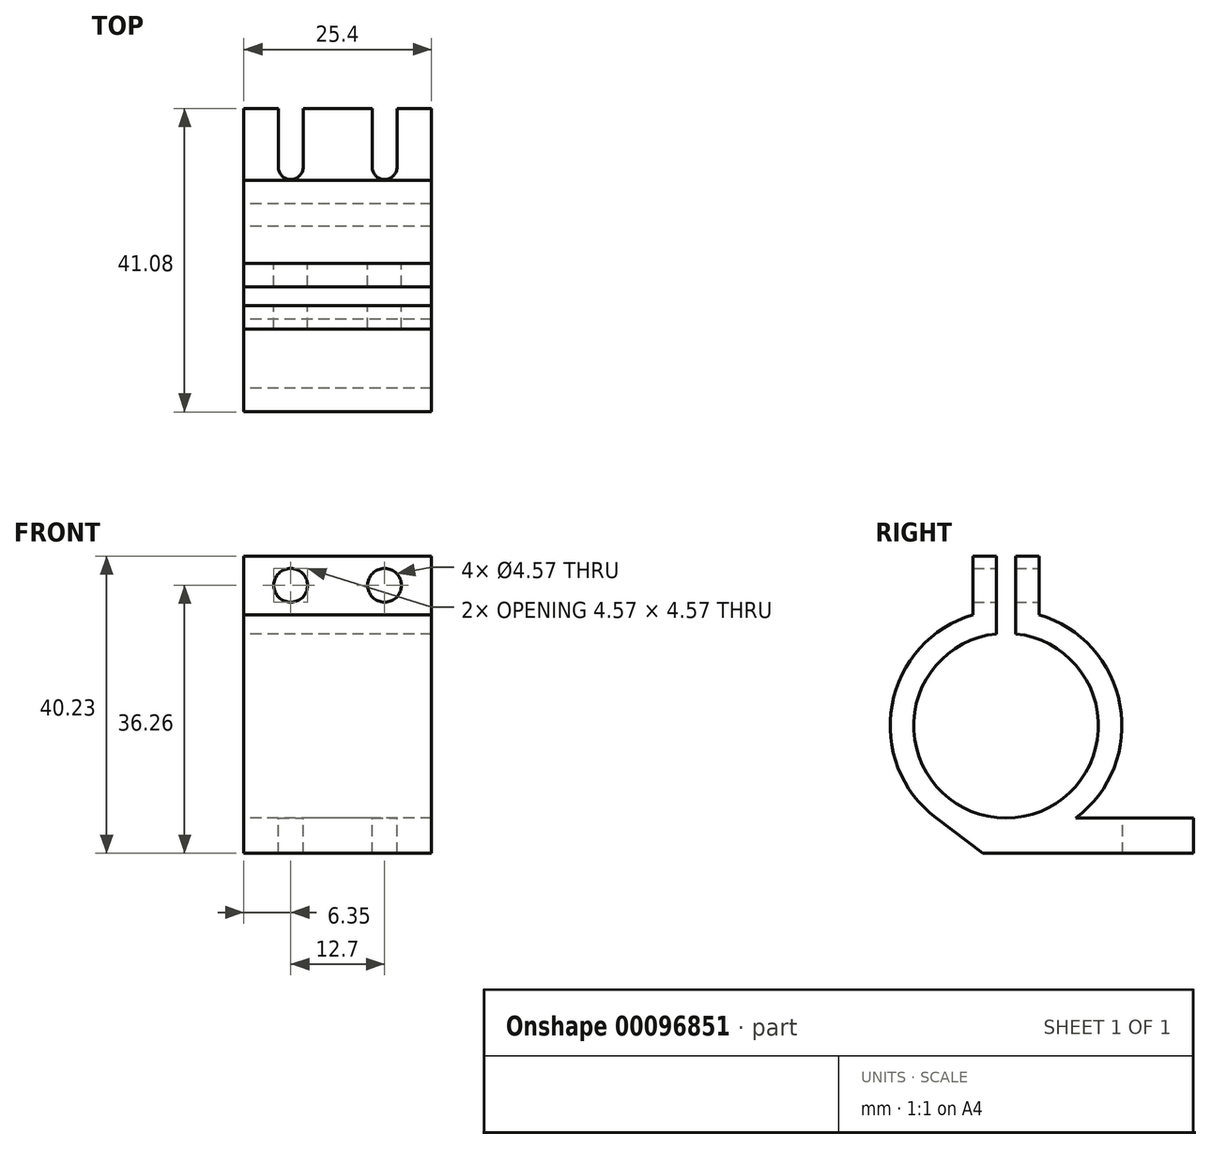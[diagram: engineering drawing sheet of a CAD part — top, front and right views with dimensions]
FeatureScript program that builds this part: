
annotation { "Feature Type Name" : "Feature", "Feature Type Description" : "" }
export const myFeature = defineFeature(function(context is Context, id is Id, definition is map)
    precondition{}
    {
        {
            var Q0;
            Q0=qCreatedBy(makeId("Right.planeOp"),FACE);
            var sketch = newSketch(context, id + "F0", { "sketchPlane" : qUnion([Q0])});
            skArc(sketch, "E0", {"start": v(-1.27, 12.44) * mm, "mid": v(0, -12.5) * mm, "end": v(1.27, 12.44) * mm});
            skLineSegment(sketch, "E1", {"start": v(-1.27, 12.44) * mm, "end": v(-1.27, 22.97) * mm});
            skLineSegment(sketch, "E2", {"start": v(-1.27, 22.97) * mm, "end": v(-4.45, 22.97) * mm});
            skLineSegment(sketch, "E3", {"start": v(-4.45, 22.97) * mm, "end": v(-4.45, 15.03) * mm});
            skLineSegment(sketch, "E4", {"start": v(1.27, 12.44) * mm, "end": v(1.27, 22.97) * mm});
            skLineSegment(sketch, "E5", {"start": v(1.27, 22.97) * mm, "end": v(4.45, 22.97) * mm});
            skLineSegment(sketch, "E6", {"start": v(4.45, 22.97) * mm, "end": v(4.45, 15.03) * mm});
            skArc(sketch, "E7", {"start": v(-4.45, 15.03) * mm, "mid": v(-15.42, 2.8) * mm, "end": v(-9.46, -12.5) * mm});
            skLineSegment(sketch, "E8", {"start": v(-9.46, -12.5) * mm, "end": v(-25.4, -12.5) * mm});
            skLineSegment(sketch, "E9", {"start": v(-25.4, -12.5) * mm, "end": v(-25.4, -17.26) * mm});
            skLineSegment(sketch, "E10", {"start": v(-25.4, -17.26) * mm, "end": v(25.4, -17.26) * mm});
            skLineSegment(sketch, "E11", {"start": v(25.4, -17.26) * mm, "end": v(25.4, -12.5) * mm});
            skLineSegment(sketch, "E12", {"start": v(25.4, -12.5) * mm, "end": v(9.46, -12.5) * mm});
            skArc(sketch, "E13", {"start": v(4.45, 15.03) * mm, "mid": v(15.42, 2.8) * mm, "end": v(9.46, -12.5) * mm});
            skSolve(sketch);
        }
        {
            var Q0;
            Q0 = qSketchRegion(id + "F0", true);
            extrude(context, id + "F1", {"entities" : qUnion([Q0]), "depth" : 25.4 * mm});
        }
        {
            var Q0;
            Q0=makeQuery(id+"F1.opExtrude","CAP_FACE",FACE,{"disambiguationData":[OSD([sQuery(id+"F0.wireOp",EDGE,"E0"),sQuery(id+"F0.wireOp",EDGE,"E1"),sQuery(id+"F0.wireOp",EDGE,"E2"),sQuery(id+"F0.wireOp",EDGE,"E3"),sQuery(id+"F0.wireOp",EDGE,"E4"),sQuery(id+"F0.wireOp",EDGE,"E5"),sQuery(id+"F0.wireOp",EDGE,"E6"),sQuery(id+"F0.wireOp",EDGE,"E7"),sQuery(id+"F0.wireOp",EDGE,"E8"),sQuery(id+"F0.wireOp",EDGE,"E9"),sQuery(id+"F0.wireOp",EDGE,"E10"),sQuery(id+"F0.wireOp",EDGE,"E11"),sQuery(id+"F0.wireOp",EDGE,"E12"),sQuery(id+"F0.wireOp",EDGE,"E13")])],"isStart":true});
            var sketch = newSketch(context, id + "F2", { "sketchPlane" : qUnion([Q0])});
            skLineSegment(sketch, "E14", {"start": v(9.46, -12.5) * mm, "end": v(3.16, -17.26) * mm});
            skLineSegment(sketch, "E15", {"start": v(3.16, -17.26) * mm, "end": v(25.4, -17.26) * mm});
            skLineSegment(sketch, "E16", {"start": v(25.4, -17.26) * mm, "end": v(25.4, -12.5) * mm});
            skLineSegment(sketch, "E17", {"start": v(25.4, -12.5) * mm, "end": v(9.46, -12.5) * mm});
            skSolve(sketch);
        }
        {
            var Q0;
            Q0=makeQuery(id+"F2.imprint","IMPRINT",FACE,{"disambiguationData":[TD([[makeQuery(id+"F2.imprint","IMPRINT",EDGE,{"derivedFrom":sQuery(id+"F2.wireOp",EDGE,"E14")}),1.0]])]});
            extrude(context, id + "F3", {"entities" : qUnion([Q0]), "operationType" : NewBodyOperationType.REMOVE, "endBound" : BoundingType.THROUGH_ALL, "oppositeDirection" : true, "depth" : 25.4 * mm});
        }
        {
            var Q0;
            Q0=makeQuery(id+"F1.opExtrude","SWEPT_FACE",FACE,{"disambiguationData":[OSD([sQuery(id+"F0.wireOp",EDGE,"E12")])]});
            var sketch = newSketch(context, id + "F4", { "sketchPlane" : qUnion([Q0])});
            skLineSegment(sketch, "E18", {"start": v(6.35, 17.46) * mm, "end": v(19.05, 17.46) * mm, "construction": true});
            skLineSegment(sketch, "E19", {"start": v(19.05, 17.46) * mm, "end": v(25.4, 17.46) * mm, "construction": true});
            skLineSegment(sketch, "E20", {"start": v(6.35, 17.46) * mm, "end": v(0, 17.46) * mm, "construction": true});
            skArc(sketch, "E21", {"start": v(4.66, 17.46) * mm, "mid": v(6.35, 15.77) * mm, "end": v(8.04, 17.46) * mm});
            skArc(sketch, "E22", {"start": v(17.36, 17.46) * mm, "mid": v(19.05, 15.77) * mm, "end": v(20.74, 17.46) * mm});
            skLineSegment(sketch, "E23", {"start": v(20.74, 17.46) * mm, "end": v(20.74, 25.4) * mm});
            skLineSegment(sketch, "E24", {"start": v(20.74, 25.4) * mm, "end": v(17.36, 25.4) * mm});
            skLineSegment(sketch, "E25", {"start": v(17.36, 25.4) * mm, "end": v(17.36, 17.46) * mm});
            skLineSegment(sketch, "E26", {"start": v(8.04, 17.46) * mm, "end": v(8.04, 25.4) * mm});
            skLineSegment(sketch, "E27", {"start": v(8.04, 25.4) * mm, "end": v(4.66, 25.4) * mm});
            skLineSegment(sketch, "E28", {"start": v(4.66, 25.4) * mm, "end": v(4.66, 17.46) * mm});
            skSolve(sketch);
        }
        {
            var Q0;
            Q0 = qSketchRegion(id + "F4", true);
            extrude(context, id + "F5", {"entities" : qUnion([Q0]), "operationType" : NewBodyOperationType.REMOVE, "endBound" : BoundingType.UP_TO_NEXT, "oppositeDirection" : true, "depth" : 25.4 * mm});
        }
        {
            var Q0;
            Q0=makeQuery(id+"F1.opExtrude","SWEPT_FACE",FACE,{"disambiguationData":[OSD([sQuery(id+"F0.wireOp",EDGE,"E6")])]});
            var sketch = newSketch(context, id + "F6", { "sketchPlane" : qUnion([Q0])});
            skLineSegment(sketch, "E29", {"start": v(-25.4, 19) * mm, "end": v(-19.05, 19) * mm, "construction": true});
            skLineSegment(sketch, "E30", {"start": v(-19.05, 19) * mm, "end": v(-6.35, 19) * mm, "construction": true});
            skLineSegment(sketch, "E31", {"start": v(-6.35, 19) * mm, "end": v(0, 19) * mm, "construction": true});
            skCircle(sketch, "E32", {"center": v(-19.05, 19) * mm, "radius": 2.29 * mm});
            skCircle(sketch, "E33", {"center": v(-6.35, 19) * mm, "radius": 2.29 * mm});
            skSolve(sketch);
        }
        {
            var Q0;
            Q0 = qSketchRegion(id + "F6", true);
            extrude(context, id + "F7", {"entities" : qUnion([Q0]), "operationType" : NewBodyOperationType.REMOVE, "endBound" : BoundingType.THROUGH_ALL, "oppositeDirection" : true, "depth" : 25.4 * mm});
        }
    });
